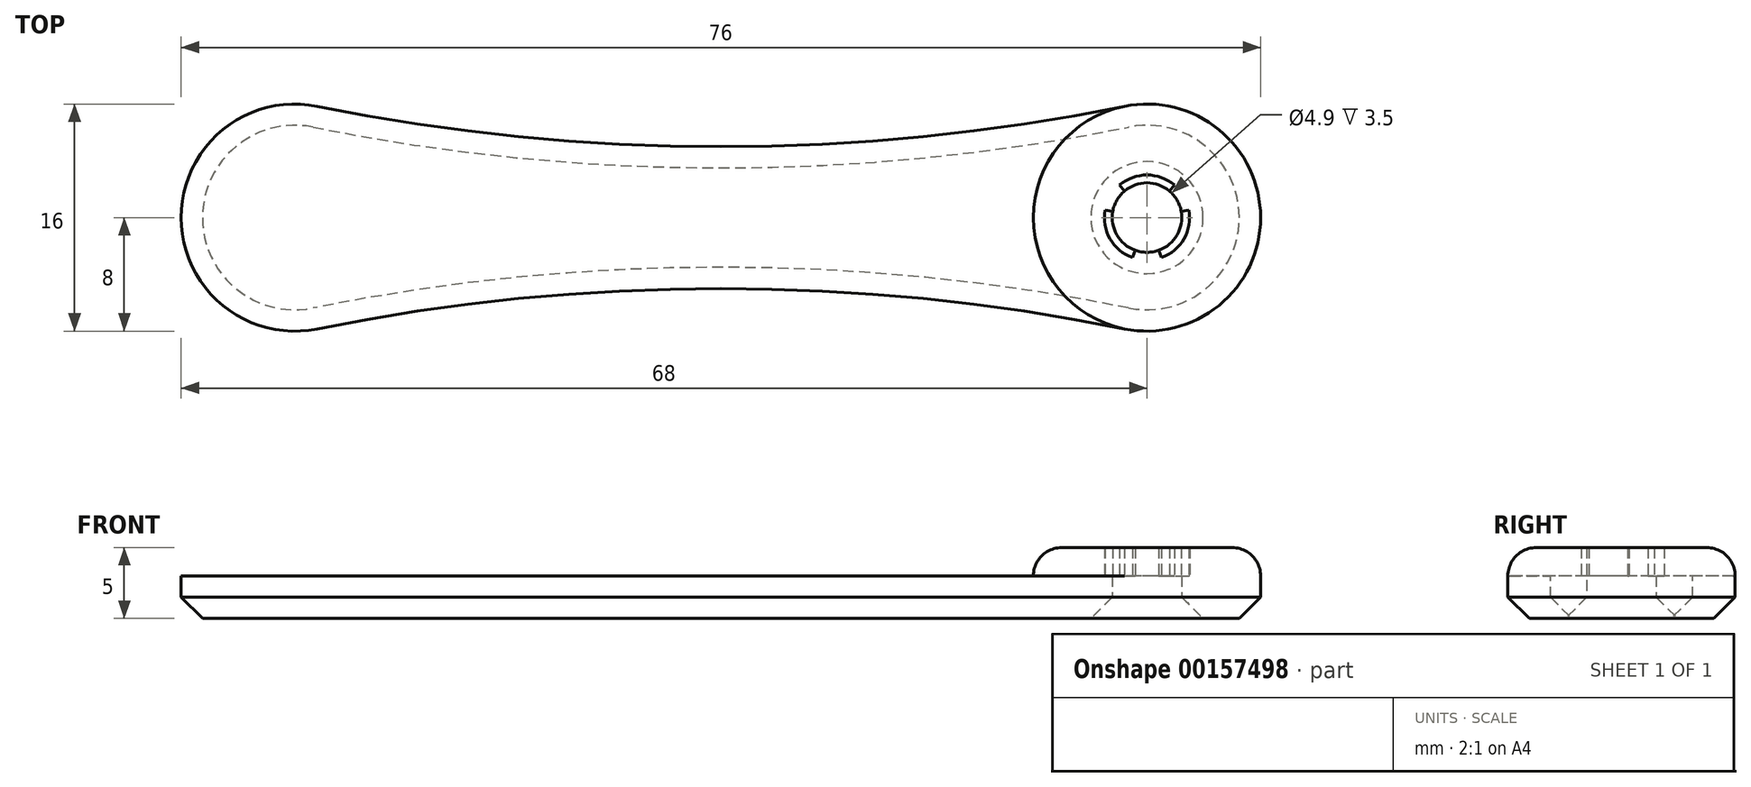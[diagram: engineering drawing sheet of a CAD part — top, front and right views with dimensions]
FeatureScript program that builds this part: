
annotation { "Feature Type Name" : "Feature", "Feature Type Description" : "" }
export const myFeature = defineFeature(function(context is Context, id is Id, definition is map)
    precondition{}
    {
        {
            var Q0;
            Q0=qCreatedBy(makeId("Top.planeOp"),FACE);
            var sketch = newSketch(context, id + "F0", { "sketchPlane" : qUnion([Q0])});
            skCircle(sketch, "E0", {"center": v(0, 0) * mm, "radius": 3 * mm});
            skCircle(sketch, "E1", {"center": v(0, 0) * mm, "radius": 8 * mm});
            skCircle(sketch, "E2", {"center": v(-60, 0) * mm, "radius": 8 * mm});
            skLineSegment(sketch, "E3", {"start": v(-60, 0) * mm, "end": v(0, 0) * mm, "construction": true});
            skPoint(sketch, "E4", {"position": v(-30, 0) * mm});
            skArc(sketch, "E5", {"start": v(-58.42, 7.84) * mm, "mid": v(-30, 5) * mm, "end": v(-1.58, 7.84) * mm});
            skArc(sketch, "E6.MirrorCS", {"start": v(-58.42, -7.84) * mm, "mid": v(-30, -5) * mm, "end": v(-1.58, -7.84) * mm});
            skLineSegment(sketch, "E7", {"start": v(-10.41, -10.25) * mm, "end": v(10.41, 10.25) * mm, "construction": true});
            skCircle(sketch, "E8", {"center": v(0, 0) * mm, "radius": 2.45 * mm});
            skLineSegment(sketch, "E9", {"start": v(0, 0) * mm, "end": v(0, -3) * mm, "construction": true});
            skLineSegment(sketch, "E10", {"start": v(0, 0) * mm, "end": v(2.6, 1.5) * mm, "construction": true});
            skLineSegment(sketch, "E11.MirrorCS", {"start": v(0, 0) * mm, "end": v(-2.6, 1.5) * mm, "construction": true});
            skLineSegment(sketch, "E12", {"start": v(0, 0) * mm, "end": v(2.95, 0.52) * mm});
            skLineSegment(sketch, "E13.MirrorCS", {"start": v(0, 0) * mm, "end": v(1.93, 2.3) * mm});
            skLineSegment(sketch, "E14.MirrorCS", {"start": v(0, 0) * mm, "end": v(-2.95, 0.52) * mm});
            skLineSegment(sketch, "E15.MirrorCS", {"start": v(0, 0) * mm, "end": v(-1.93, 2.3) * mm});
            skLineSegment(sketch, "E16", {"start": v(0, 0) * mm, "end": v(-1.03, -2.82) * mm});
            skLineSegment(sketch, "E17.MirrorCS", {"start": v(0, 0) * mm, "end": v(1.03, -2.82) * mm});
            skSolve(sketch);
        }
        {
            var Q0;
            {var subQ0=sQuery(id+"F0.wireOp",EDGE,"E5");Q0=makeQuery(id+"F0.imprint","IMPRINT",FACE,{"disambiguationData":[TD([[makeQuery(id+"F0.imprint","IMPRINT",EDGE,{"derivedFrom":subQ0}),-1.0]])]});}
            var Q1;
            {var subQ0=sQuery(id+"F0.wireOp",EDGE,"E2");var subQ1=makeQuery(id+"F0.imprint","INTERSECT",VERTEX,{"derivedFrom":[subQ0,sQuery(id+"F0.wireOp",EDGE,"E5")]});Q1=makeQuery(id+"F0.imprint","IMPRINT",FACE,{"disambiguationData":[TD([[makeQuery(id+"F0.imprint","IMPRINT",EDGE,{"disambiguationData":[TD([[subQ1,-1.0]])],"derivedFrom":subQ0}),1.0]])]});}
            var Q2;
            {var subQ0=sQuery(id+"F0.wireOp",EDGE,"3BCd2sIu-g8Cj-2UkR-eEc3-04YAKtrgslWz");var subQ1=sQuery(id+"F0.wireOp",EDGE,"E0");var subQ2=makeQuery(id+"F0.imprint","INTERSECT",VERTEX,{"disambiguationData":[OD(0.0)],"derivedFrom":[subQ1,subQ0]});Q2=makeQuery(id+"F0.imprint","IMPRINT",FACE,{"disambiguationData":[TD([[makeQuery(id+"F0.imprint","IMPRINT",EDGE,{"disambiguationData":[TD([[subQ2,1.0]])],"derivedFrom":subQ1}),-1.0]])]});}
            var Q3;
            {var subQ0=sQuery(id+"F0.wireOp",EDGE,"3BCd2sIu-g8Cj-2UkR-eEc3-04YAKtrgslWz");Q3=makeQuery(id+"F0.imprint","IMPRINT",FACE,{"disambiguationData":[TD([[makeQuery(id+"F0.imprint","IMPRINT",EDGE,{"derivedFrom":subQ0}),1.0]])]});}
            var Q4;
            {var subQ0=sQuery(id+"F0.wireOp",EDGE,"3BCd2sIu-g8Cj-2UkR-eEc3-04YAKtrgslWz");Q4=makeQuery(id+"F0.imprint","IMPRINT",FACE,{"disambiguationData":[TD([[makeQuery(id+"F0.imprint","IMPRINT",EDGE,{"derivedFrom":subQ0}),-1.0]])]});}
            var Q5;
            {var subQ0=sQuery(id+"F0.wireOp",EDGE,"E14.MirrorCS");var subQ1=sQuery(id+"F0.wireOp",EDGE,"E8");var subQ2=makeQuery(id+"F0.imprint","INTERSECT",VERTEX,{"derivedFrom":[subQ1,subQ0]});Q5=makeQuery(id+"F0.imprint","IMPRINT",FACE,{"disambiguationData":[TD([[makeQuery(id+"F0.imprint","IMPRINT",EDGE,{"disambiguationData":[TD([[subQ2,-1.0]])],"derivedFrom":subQ1}),1.0]])]});}
            var Q6;
            {var subQ0=sQuery(id+"F0.wireOp",EDGE,"E14.MirrorCS");var subQ1=sQuery(id+"F0.wireOp",EDGE,"E0");var subQ2=makeQuery(id+"F0.imprint","INTERSECT",VERTEX,{"derivedFrom":[subQ1,subQ0]});Q6=makeQuery(id+"F0.imprint","IMPRINT",FACE,{"disambiguationData":[TD([[makeQuery(id+"F0.imprint","IMPRINT",EDGE,{"disambiguationData":[TD([[subQ2,-1.0]])],"derivedFrom":subQ1}),1.0]])]});}
            var Q7;
            {var subQ0=sQuery(id+"F0.wireOp",EDGE,"E14.MirrorCS");var subQ1=sQuery(id+"F0.wireOp",EDGE,"E0");var subQ2=makeQuery(id+"F0.imprint","INTERSECT",VERTEX,{"derivedFrom":[subQ1,subQ0]});Q7=makeQuery(id+"F0.imprint","IMPRINT",FACE,{"disambiguationData":[TD([[makeQuery(id+"F0.imprint","IMPRINT",EDGE,{"disambiguationData":[TD([[subQ2,1.0]])],"derivedFrom":subQ1}),1.0]])]});}
            var Q8;
            {var subQ0=sQuery(id+"F0.wireOp",EDGE,"E13.MirrorCS");var subQ1=sQuery(id+"F0.wireOp",EDGE,"E0");var subQ2=makeQuery(id+"F0.imprint","INTERSECT",VERTEX,{"derivedFrom":[subQ1,subQ0]});Q8=makeQuery(id+"F0.imprint","IMPRINT",FACE,{"disambiguationData":[TD([[makeQuery(id+"F0.imprint","IMPRINT",EDGE,{"disambiguationData":[TD([[subQ2,-1.0]])],"derivedFrom":subQ1}),1.0]])]});}
            var Q9;
            {var subQ0=sQuery(id+"F0.wireOp",EDGE,"E12");var subQ1=sQuery(id+"F0.wireOp",EDGE,"E0");var subQ2=makeQuery(id+"F0.imprint","INTERSECT",VERTEX,{"derivedFrom":[subQ1,subQ0]});Q9=makeQuery(id+"F0.imprint","IMPRINT",FACE,{"disambiguationData":[TD([[makeQuery(id+"F0.imprint","IMPRINT",EDGE,{"disambiguationData":[TD([[subQ2,-1.0]])],"derivedFrom":subQ1}),1.0]])]});}
            var Q10;
            {var subQ0=sQuery(id+"F0.wireOp",EDGE,"E12");var subQ1=sQuery(id+"F0.wireOp",EDGE,"E0");var subQ2=makeQuery(id+"F0.imprint","INTERSECT",VERTEX,{"derivedFrom":[subQ1,subQ0]});Q10=makeQuery(id+"F0.imprint","IMPRINT",FACE,{"disambiguationData":[TD([[makeQuery(id+"F0.imprint","IMPRINT",EDGE,{"disambiguationData":[TD([[subQ2,1.0]])],"derivedFrom":subQ1}),1.0]])]});}
            var Q11;
            {var subQ0=sQuery(id+"F0.wireOp",EDGE,"E12");var subQ1=sQuery(id+"F0.wireOp",EDGE,"E8");var subQ2=makeQuery(id+"F0.imprint","INTERSECT",VERTEX,{"derivedFrom":[subQ1,subQ0]});Q11=makeQuery(id+"F0.imprint","IMPRINT",FACE,{"disambiguationData":[TD([[makeQuery(id+"F0.imprint","IMPRINT",EDGE,{"disambiguationData":[TD([[subQ2,1.0]])],"derivedFrom":subQ1}),1.0]])]});}
            var Q12;
            {var subQ0=sQuery(id+"F0.wireOp",EDGE,"E16");var subQ1=sQuery(id+"F0.wireOp",EDGE,"E0");var subQ2=makeQuery(id+"F0.imprint","INTERSECT",VERTEX,{"derivedFrom":[subQ1,subQ0]});Q12=makeQuery(id+"F0.imprint","IMPRINT",FACE,{"disambiguationData":[TD([[makeQuery(id+"F0.imprint","IMPRINT",EDGE,{"disambiguationData":[TD([[subQ2,-1.0]])],"derivedFrom":subQ1}),1.0]])]});}
            var Q13;
            {var subQ0=sQuery(id+"F0.wireOp",EDGE,"E16");var subQ1=sQuery(id+"F0.wireOp",EDGE,"E8");var subQ2=makeQuery(id+"F0.imprint","INTERSECT",VERTEX,{"derivedFrom":[subQ1,subQ0]});Q13=makeQuery(id+"F0.imprint","IMPRINT",FACE,{"disambiguationData":[TD([[makeQuery(id+"F0.imprint","IMPRINT",EDGE,{"disambiguationData":[TD([[subQ2,-1.0]])],"derivedFrom":subQ1}),1.0]])]});}
            var Q14;
            {var subQ0=sQuery(id+"F0.wireOp",EDGE,"E15.MirrorCS");var subQ1=sQuery(id+"F0.wireOp",EDGE,"E8");var subQ2=makeQuery(id+"F0.imprint","INTERSECT",VERTEX,{"derivedFrom":[subQ1,subQ0]});Q14=makeQuery(id+"F0.imprint","IMPRINT",FACE,{"disambiguationData":[TD([[makeQuery(id+"F0.imprint","IMPRINT",EDGE,{"disambiguationData":[TD([[subQ2,-1.0]])],"derivedFrom":subQ1}),1.0]])]});}
            var Q15;
            {var subQ0=sQuery(id+"F0.wireOp",EDGE,"E13.MirrorCS");var subQ1=sQuery(id+"F0.wireOp",EDGE,"E8");var subQ2=makeQuery(id+"F0.imprint","INTERSECT",VERTEX,{"derivedFrom":[subQ1,subQ0]});Q15=makeQuery(id+"F0.imprint","IMPRINT",FACE,{"disambiguationData":[TD([[makeQuery(id+"F0.imprint","IMPRINT",EDGE,{"disambiguationData":[TD([[subQ2,-1.0]])],"derivedFrom":subQ1}),1.0]])]});}
            var Q16;
            {var subQ0=sQuery(id+"F0.wireOp",EDGE,"E13.MirrorCS");var subQ1=sQuery(id+"F0.wireOp",EDGE,"E8");var subQ2=makeQuery(id+"F0.imprint","INTERSECT",VERTEX,{"derivedFrom":[subQ1,subQ0]});Q16=makeQuery(id+"F0.imprint","IMPRINT",FACE,{"disambiguationData":[TD([[makeQuery(id+"F0.imprint","IMPRINT",EDGE,{"disambiguationData":[TD([[subQ2,1.0]])],"derivedFrom":subQ1}),1.0]])]});}
            extrude(context, id + "F1", {"entities" : qUnion([Q0, Q1, Q2, Q3, Q4, Q5, Q6, Q7, Q8, Q9, Q10, Q11, Q12, Q13, Q14, Q15, Q16]), "oppositeDirection" : true, "depth" : 3 * mm});
        }
        {
            var Q0;
            {var subQ0=sQuery(id+"F0.wireOp",EDGE,"3BCd2sIu-g8Cj-2UkR-eEc3-04YAKtrgslWz");var subQ1=sQuery(id+"F0.wireOp",EDGE,"E0");var subQ2=makeQuery(id+"F0.imprint","INTERSECT",VERTEX,{"disambiguationData":[OD(0.0)],"derivedFrom":[subQ1,subQ0]});Q0=makeQuery(id+"F0.imprint","IMPRINT",FACE,{"disambiguationData":[TD([[makeQuery(id+"F0.imprint","IMPRINT",EDGE,{"disambiguationData":[TD([[subQ2,1.0]])],"derivedFrom":subQ1}),-1.0]])]});}
            var Q1;
            {var subQ0=sQuery(id+"F0.wireOp",EDGE,"3BCd2sIu-g8Cj-2UkR-eEc3-04YAKtrgslWz");Q1=makeQuery(id+"F0.imprint","IMPRINT",FACE,{"disambiguationData":[TD([[makeQuery(id+"F0.imprint","IMPRINT",EDGE,{"derivedFrom":subQ0}),-1.0]])]});}
            var Q2;
            {var subQ0=sQuery(id+"F0.wireOp",EDGE,"E14.MirrorCS");var subQ1=sQuery(id+"F0.wireOp",EDGE,"E0");var subQ2=makeQuery(id+"F0.imprint","INTERSECT",VERTEX,{"derivedFrom":[subQ1,subQ0]});Q2=makeQuery(id+"F0.imprint","IMPRINT",FACE,{"disambiguationData":[TD([[makeQuery(id+"F0.imprint","IMPRINT",EDGE,{"disambiguationData":[TD([[subQ2,1.0]])],"derivedFrom":subQ1}),1.0]])]});}
            var Q3;
            {var subQ0=sQuery(id+"F0.wireOp",EDGE,"E12");var subQ1=sQuery(id+"F0.wireOp",EDGE,"E0");var subQ2=makeQuery(id+"F0.imprint","INTERSECT",VERTEX,{"derivedFrom":[subQ1,subQ0]});Q3=makeQuery(id+"F0.imprint","IMPRINT",FACE,{"disambiguationData":[TD([[makeQuery(id+"F0.imprint","IMPRINT",EDGE,{"disambiguationData":[TD([[subQ2,-1.0]])],"derivedFrom":subQ1}),1.0]])]});}
            var Q4;
            {var subQ0=sQuery(id+"F0.wireOp",EDGE,"E16");var subQ1=sQuery(id+"F0.wireOp",EDGE,"E0");var subQ2=makeQuery(id+"F0.imprint","INTERSECT",VERTEX,{"derivedFrom":[subQ1,subQ0]});Q4=makeQuery(id+"F0.imprint","IMPRINT",FACE,{"disambiguationData":[TD([[makeQuery(id+"F0.imprint","IMPRINT",EDGE,{"disambiguationData":[TD([[subQ2,-1.0]])],"derivedFrom":subQ1}),1.0]])]});}
            extrude(context, id + "F2", {"entities" : qUnion([Q0, Q1, Q2, Q3, Q4]), "operationType" : NewBodyOperationType.ADD, "depth" : 2 * mm});
        }
        {
            var Q0;
            Q0=makeQuery(id+"F1.opExtrude","CAP_EDGE",EDGE,{"disambiguationData":[OSD([sQuery(id+"F0.wireOp",EDGE,"E5")])],"isStart":false});
            chamfer(context, id + "F3", {"entities" : qUnion([Q0]), "width" : 1.5 * mm, "tangentPropagation" : true});
        }
        {
            var Q0;
            {var subQ2=sQuery(id+"F0.wireOp",EDGE,"E12");Q0=makeQuery(id+"F2.boolean.opBoolean","SPLIT",FACE,{"disambiguationData":[TD([makeQuery(id+"F2.opExtrude","SWEPT_FACE",FACE,{"disambiguationData":[OSD([subQ2])]})])],"derivedFrom":makeQuery(id+"F1.opExtrude","CAP_FACE",FACE,{"disambiguationData":[OSD([sQuery(id+"F0.wireOp",EDGE,"E1"),sQuery(id+"F0.wireOp",EDGE,"E2"),sQuery(id+"F0.wireOp",EDGE,"E5"),sQuery(id+"F0.wireOp",EDGE,"E6.MirrorCS")])],"isStart":true})});}
            var sketch = newSketch(context, id + "F4", { "sketchPlane" : qUnion([Q0])});
            skCircle(sketch, "E18", {"center": v(0, 0) * mm, "radius": 2.45 * mm});
            skSolve(sketch);
        }
        {
            var Q0;
            {var subQ0=sQuery(id+"F4.wireOp",EDGE,"E18");var subQ3=makeQuery(id+"F4.imprint","INTERSECT",VERTEX,{"derivedFrom":[makeQuery(id+"F2.opExtrude","CAP_EDGE",EDGE,{"disambiguationData":[OSD([sQuery(id+"F0.wireOp",EDGE,"E13.MirrorCS")])],"isStart":true}),subQ0]});Q0=makeQuery(id+"F4.imprint","IMPRINT",FACE,{"disambiguationData":[TD([[makeQuery(id+"F4.imprint","IMPRINT",EDGE,{"disambiguationData":[TD([[subQ3,1.0]])],"derivedFrom":subQ0}),1.0]])]});}
            extrude(context, id + "F5", {"entities" : qUnion([Q0]), "operationType" : NewBodyOperationType.REMOVE, "oppositeDirection" : true, "depth" : 25 * mm});
        }
        {
            var Q0;
            Q0=makeQuery(id+"F5.boolean.opBoolean","INTERSECT",EDGE,{"derivedFrom":[makeQuery(id+"F1.opExtrude","CAP_FACE",FACE,{"disambiguationData":[OSD([sQuery(id+"F0.wireOp",EDGE,"E1"),sQuery(id+"F0.wireOp",EDGE,"E2"),sQuery(id+"F0.wireOp",EDGE,"E5"),sQuery(id+"F0.wireOp",EDGE,"E6.MirrorCS")])],"isStart":false}),makeQuery(id+"F5.opExtrude","SWEPT_FACE",FACE,{"disambiguationData":[OSD([sQuery(id+"F4.wireOp",EDGE,"E18")])]})]});
            chamfer(context, id + "F6", {"entities" : qUnion([Q0]), "width" : 1.5 * mm, "tangentPropagation" : true});
        }
        {
            var Q0;
            Q0=makeQuery(id+"F2.opExtrude","CAP_EDGE",EDGE,{"disambiguationData":[OSD([sQuery(id+"F0.wireOp",EDGE,"E1")])],"isStart":false});
            fillet(context, id + "F7", {"entities" : qUnion([Q0]), "radius" : 2 * mm, "tangentPropagation" : true, "allowEdgeOverflow" : false});
        }
    });
